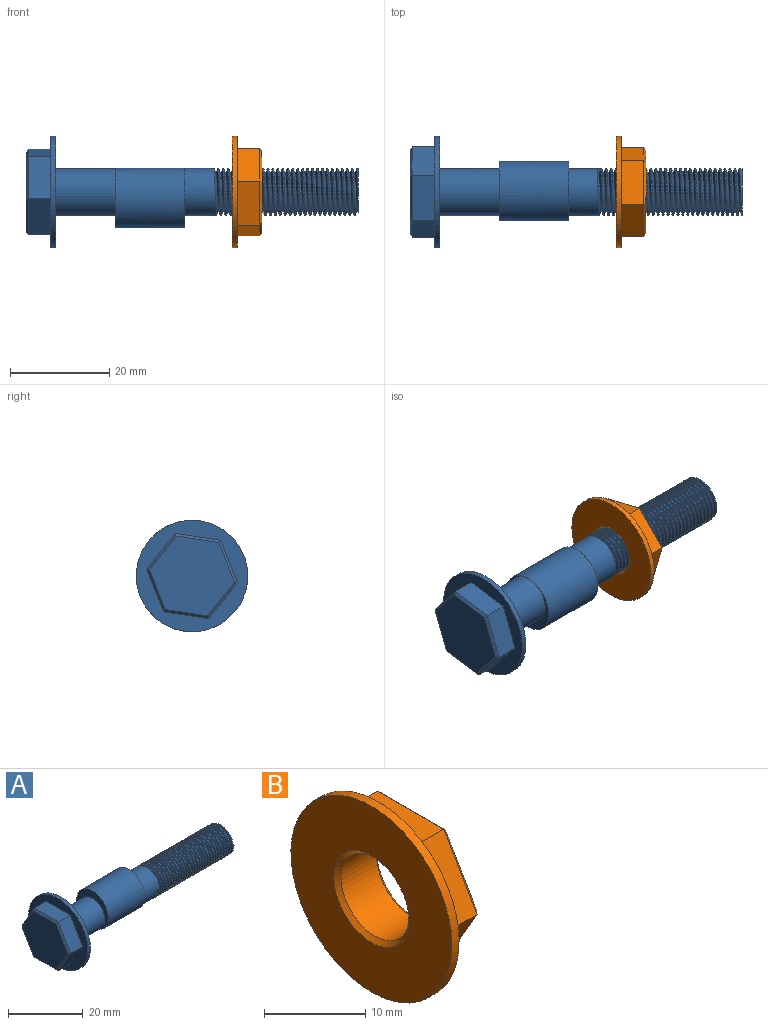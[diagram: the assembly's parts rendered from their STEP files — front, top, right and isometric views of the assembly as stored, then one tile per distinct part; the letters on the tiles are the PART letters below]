
ASSEMBLY  parts=2 mates=1
PART A: 55 faces, bbox 91.5x46.5x46.5 mm
  f0: plane 8x4.62mm, normal (0,0.87,-0.5), area 41.6mm2, adj f1,f5,f8,f54
  f1: plane 8x4.62mm, normal (0,0.87,0.5), area 41.6mm2, adj f0,f2,f8,f53
  f2: plane 9.24x4.5mm, normal (0,0,1), area 41.6mm2, adj f1,f3,f8,f51
  f3: plane 8x4.62mm, normal (0,-0.87,0.5), area 41.6mm2, adj f2,f4,f8,f49
  f4: plane 8x4.62mm, normal (0,-0.87,-0.5), area 41.6mm2, adj f3,f5,f8,f50
  f5: plane 9.24x4.5mm, normal (0,0,-1), area 41.6mm2, adj f0,f4,f8,f52
  f6: plane 17.32x15mm, normal (-1,0,0), area 194.9mm2, adj f49,f50,f51,f52,f53,f54
  f7: plane 22.48x22.48mm, normal (1,0,0), area 325.8mm2, adj f9,f44
  f8: plane 22.48x22.48mm, normal (-1,0,0), area 175mm2, adj f0,f1,f2,f3,f4,f5,f9
  f9: cylinder r=11.24mm len=22.48mm, axis (1,0,0), area 70.6mm2, adj f7,f8
  f10: plane 10.13x9.53mm, normal (1,0,0), area 63mm2, adj f40,f46,f47,f48
  f11: cylinder r=4.75mm len=9.5mm, axis (-1,0,0), area 185mm2, adj f12,f42,f45,f47
  f12: cylinder r=4.75mm len=9.5mm, axis (-1,0,0), area 6mm2, adj f11,f13,f47,f48
  f13: cylinder r=4.75mm len=9.5mm, axis (-1,0,0), area 6mm2, adj f12,f14,f47,f48
  f14: cylinder r=4.75mm len=9.5mm, axis (-1,0,0), area 6mm2, adj f13,f15,f47,f48
  f15: cylinder r=4.75mm len=9.5mm, axis (-1,0,0), area 6mm2, adj f14,f16,f47,f48
  f16: cylinder r=4.75mm len=9.5mm, axis (-1,0,0), area 6mm2, adj f15,f17,f47,f48
  f17: cylinder r=4.75mm len=9.5mm, axis (-1,0,0), area 6mm2, adj f16,f18,f47,f48
  f18: cylinder r=4.75mm len=9.5mm, axis (-1,0,0), area 6mm2, adj f17,f19,f47,f48
  f19: cylinder r=4.75mm len=9.5mm, axis (-1,0,0), area 6mm2, adj f18,f20,f47,f48
  f20: cylinder r=4.75mm len=9.5mm, axis (-1,0,0), area 6mm2, adj f19,f21,f47,f48
  f21: cylinder r=4.75mm len=9.5mm, axis (-1,0,0), area 6mm2, adj f20,f22,f47,f48
  f22: cylinder r=4.75mm len=9.5mm, axis (-1,0,0), area 6mm2, adj f21,f23,f47,f48
  f23: cylinder r=4.75mm len=9.5mm, axis (-1,0,0), area 6mm2, adj f22,f24,f47,f48
  f24: cylinder r=4.75mm len=9.5mm, axis (-1,0,0), area 6mm2, adj f23,f25,f47,f48
  f25: cylinder r=4.75mm len=9.5mm, axis (-1,0,0), area 6mm2, adj f24,f26,f47,f48
  f26: cylinder r=4.75mm len=9.5mm, axis (-1,0,0), area 6mm2, adj f25,f27,f47,f48
  f27: cylinder r=4.75mm len=9.5mm, axis (-1,0,0), area 6mm2, adj f26,f28,f47,f48
  f28: cylinder r=4.75mm len=9.5mm, axis (-1,0,0), area 6mm2, adj f27,f29,f47,f48
  f29: cylinder r=4.75mm len=9.5mm, axis (-1,0,0), area 6mm2, adj f28,f30,f47,f48
  f30: cylinder r=4.75mm len=9.5mm, axis (-1,0,0), area 6mm2, adj f29,f31,f47,f48
  f31: cylinder r=4.75mm len=9.5mm, axis (-1,0,0), area 6mm2, adj f30,f32,f47,f48
  f32: cylinder r=4.75mm len=9.5mm, axis (-1,0,0), area 6mm2, adj f31,f33,f47,f48
  f33: cylinder r=4.75mm len=9.5mm, axis (-1,0,0), area 6mm2, adj f32,f34,f47,f48
  f34: cylinder r=4.75mm len=9.5mm, axis (-1,0,0), area 6mm2, adj f33,f35,f47,f48
  f35: cylinder r=4.75mm len=9.5mm, axis (-1,0,0), area 6mm2, adj f34,f36,f47,f48
  f36: cylinder r=4.75mm len=9.5mm, axis (-1,0,0), area 6mm2, adj f35,f37,f47,f48
  f37: cylinder r=4.75mm len=9.5mm, axis (-1,0,0), area 6mm2, adj f36,f38,f47,f48
  f38: cylinder r=4.75mm len=9.5mm, axis (-1,0,0), area 6mm2, adj f37,f39,f47,f48
  f39: cylinder r=4.75mm len=9.5mm, axis (-1,0,0), area 6mm2, adj f38,f40,f47,f48
  f40: cylinder r=4.75mm len=9.5mm, axis (-1,0,0), area 3.7mm2, adj f10,f39,f46,f48
  f41: plane 36x36mm, normal (-1,0,0), area 155.3mm2, adj f43,f44
  f42: plane 12x12mm, normal (1,0,0), area 42.2mm2, adj f11,f43
  f43: cylinder r=6mm len=14mm, axis (-1,0,0), area 527.8mm2, adj f41,f42
  f44: cylinder r=4.75mm len=12mm, axis (-1,0,0), area 358.1mm2, adj f7,f41
  f45: plane 1x0.8mm, normal (0,0,-1), area 0.4mm2, adj f11,f47,f48
  f46: plane 0.75x0.3mm, normal (0,0,1), area 0.1mm2, adj f10,f40,f47
  f47: bspline ~29.4x10.97mm, area 838.4mm2, adj f10,f11,f12,f13,f14,f15,f16,f17
  f48: bspline ~29.4x10.97mm, area 825.7mm2, adj f10,f12,f13,f14,f15,f16,f17,f18
  f49: plane 8x4.91mm, normal (-0.71,-0.61,0.35), area 6.3mm2, adj f3,f6,f50,f51
  f50: plane 8x4.91mm, normal (-0.71,-0.61,-0.35), area 6.3mm2, adj f4,f6,f49,f52
  f51: plane 9.24x0.5mm, normal (-0.71,0,0.71), area 6.3mm2, adj f2,f6,f49,f53
  f52: plane 9.24x0.5mm, normal (-0.71,0,-0.71), area 6.3mm2, adj f5,f6,f50,f54
  f53: plane 8x4.91mm, normal (-0.71,0.61,0.35), area 6.3mm2, adj f1,f6,f51,f54
  f54: plane 8x4.91mm, normal (-0.71,0.61,-0.35), area 6.3mm2, adj f0,f6,f52,f53
PART B: 19 faces, bbox 6x22.5x22.5 mm
  f0: plane 8x4.62mm, normal (0,0.87,-0.5), area 41.6mm2, adj f1,f6,f9,f18
  f1: plane 8x4.62mm, normal (0,0.87,0.5), area 41.6mm2, adj f0,f2,f9,f17
  f2: plane 9.24x4.5mm, normal (0,0,1), area 41.6mm2, adj f1,f3,f9,f15
  f3: plane 8x4.62mm, normal (0,-0.87,0.5), area 41.6mm2, adj f2,f4,f9,f13
  f4: plane 8x4.62mm, normal (0,-0.87,-0.5), area 41.6mm2, adj f3,f6,f9,f14
  f5: cylinder r=4.75mm len=9.5mm, axis (-1,0,0), area 149.2mm2, adj f11,f12
  f6: plane 9.24x4.5mm, normal (0,0,-1), area 41.6mm2, adj f0,f4,f9,f16
  f7: plane 17.32x15mm, normal (1,0,0), area 108.3mm2, adj f12,f13,f14,f15,f16,f17,f18
  f8: plane 22.48x22.48mm, normal (-1,0,0), area 310.1mm2, adj f10,f11
  f9: plane 22.48x22.48mm, normal (1,0,0), area 175mm2, adj f0,f1,f2,f3,f4,f6,f10
  f10: cylinder r=11.24mm len=22.48mm, axis (-1,0,0), area 70.6mm2, adj f8,f9
  f11: cone r=5.25mm half-angle=45deg, axis (-1,0,0), area 22.2mm2, adj f5,f8
  f12: cone r=4.75mm half-angle=45deg, axis (1,0,0), area 22.2mm2, adj f5,f7
  f13: plane 8x4.91mm, normal (0.71,-0.61,0.35), area 6.3mm2, adj f3,f7,f14,f15
  f14: plane 8x4.91mm, normal (0.71,-0.61,-0.35), area 6.3mm2, adj f4,f7,f13,f16
  f15: plane 9.24x0.5mm, normal (0.71,0,0.71), area 6.3mm2, adj f2,f7,f13,f17
  f16: plane 9.24x0.5mm, normal (0.71,0,-0.71), area 6.3mm2, adj f6,f7,f14,f18
  f17: plane 8x4.91mm, normal (0.71,0.61,0.35), area 6.3mm2, adj f1,f7,f15,f18
  f18: plane 8x4.91mm, normal (0.71,0.61,-0.35), area 6.3mm2, adj f0,f7,f16,f17
PLACE A rot(axis=(-1,0,0),171.4deg) t=(-2.86,-3.86,3.17)mm
PLACE B rot(axis=(1,0,0),166.1deg) t=(-22.23,-3.86,3.17)mm fixed
MATE cylindrical A.f9 <-> B.f5  axis (1,0,0) through (-2.86,-3.86,3.17)mm
